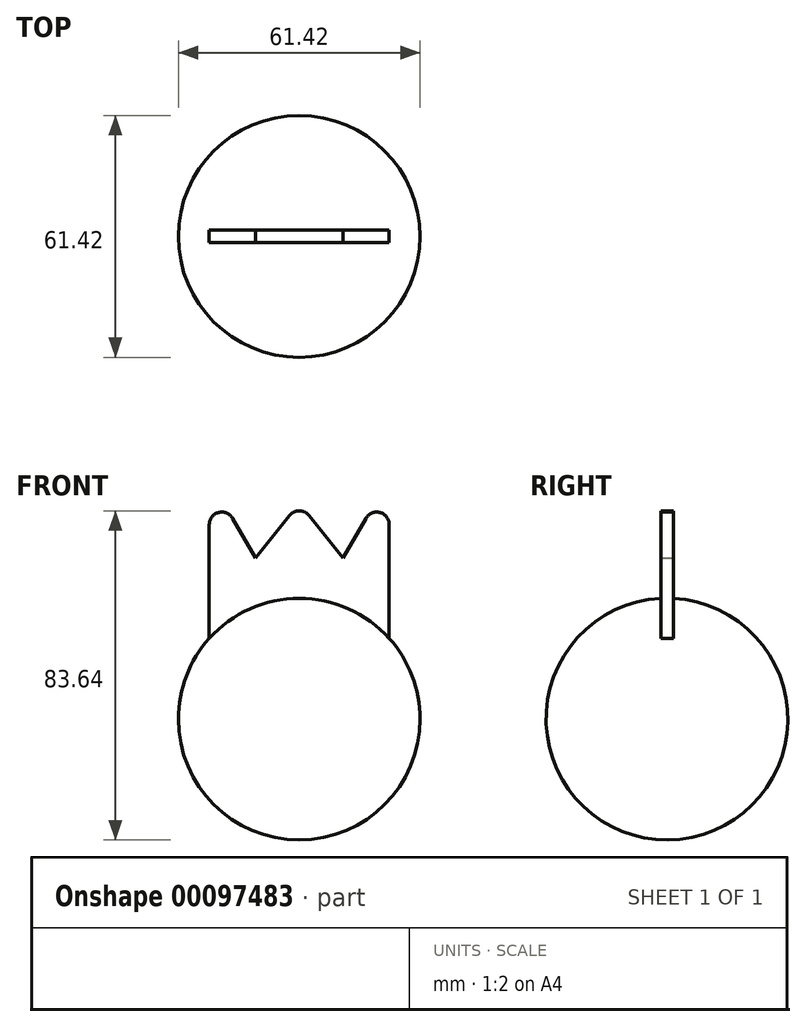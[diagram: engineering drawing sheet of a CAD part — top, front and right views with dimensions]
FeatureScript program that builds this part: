
annotation { "Feature Type Name" : "Feature", "Feature Type Description" : "" }
export const myFeature = defineFeature(function(context is Context, id is Id, definition is map)
    precondition{}
    {
        {
            var Q0;
            Q0=qCreatedBy(makeId("Front.planeOp"),FACE);
            var sketch = newSketch(context, id + "F0", { "sketchPlane" : qUnion([Q0])});
            skArc(sketch, "E0", {"start": v(-30.71, 0) * mm, "mid": v(0, 30.71) * mm, "end": v(30.71, 0) * mm});
            skLineSegment(sketch, "E1", {"start": v(-30.71, 0) * mm, "end": v(30.71, 0) * mm});
            skSolve(sketch);
        }
        {
            var Q0;
            Q0 = qSketchRegion(id + "F0", true);
            var Q1;
            Q1=sQuery(id+"F0.wireOp",EDGE,"E1");
            revolve(context, id + "F1", {"entities" : qUnion([Q0]), "axis" : qUnion([Q1]), "revolveType" : RevolveType.FULL});
        }
        {
            var Q0;
            Q0=qCreatedBy(makeId("Front.planeOp"),FACE);
            var sketch = newSketch(context, id + "F2", { "sketchPlane" : qUnion([Q0])});
            skLineSegment(sketch, "E2", {"start": v(-22.86, 15.59) * mm, "end": v(-22.86, 61.17) * mm});
            skLineSegment(sketch, "E3", {"start": v(-22.86, 61.17) * mm, "end": v(-11.08, 40.99) * mm});
            skLineSegment(sketch, "E4", {"start": v(-11.08, 40.99) * mm, "end": v(0, 54.84) * mm});
            skLineSegment(sketch, "E5.MirrorCS", {"start": v(11.08, 40.99) * mm, "end": v(0, 54.84) * mm});
            skLineSegment(sketch, "E6.MirrorCS", {"start": v(22.86, 61.17) * mm, "end": v(11.08, 40.99) * mm});
            skLineSegment(sketch, "E7.MirrorCS", {"start": v(22.86, 15.59) * mm, "end": v(22.86, 61.17) * mm});
            skLineSegment(sketch, "E8", {"start": v(-22.86, 15.59) * mm, "end": v(22.86, 15.59) * mm});
            skSolve(sketch);
        }
        {
            var Q0;
            Q0=makeQuery(id+"F2.imprint","IMPRINT",FACE,{"disambiguationData":[TD([[makeQuery(id+"F2.imprint","IMPRINT",EDGE,{"derivedFrom":sQuery(id+"F2.wireOp",EDGE,"E2")}),-1.0]])]});
            extrude(context, id + "F3", {"entities" : qUnion([Q0]), "operationType" : NewBodyOperationType.ADD, "endBound" : BoundingType.SYMMETRIC, "depth" : 3.17 * mm});
        }
        {
            var Q0;
            Q0=makeQuery(id+"F3.opExtrude","SWEPT_EDGE",EDGE,{"disambiguationData":[OSD([sQuery(id+"F2.wireOp",EDGE,"E2"),sQuery(id+"F2.wireOp",EDGE,"E3")])]});
            var Q1;
            Q1=makeQuery(id+"F3.opExtrude","SWEPT_EDGE",EDGE,{"disambiguationData":[OSD([sQuery(id+"F2.wireOp",EDGE,"E4"),sQuery(id+"F2.wireOp",EDGE,"E5.MirrorCS")])]});
            var Q2;
            Q2=makeQuery(id+"F3.opExtrude","SWEPT_EDGE",EDGE,{"disambiguationData":[OSD([sQuery(id+"F2.wireOp",EDGE,"E6.MirrorCS"),sQuery(id+"F2.wireOp",EDGE,"E7.MirrorCS")])]});
            fillet(context, id + "F4", {"entities" : qUnion([Q0, Q1, Q2]), "radius" : 3.17 * mm, "tangentPropagation" : true, "allowEdgeOverflow" : false});
        }
    });
